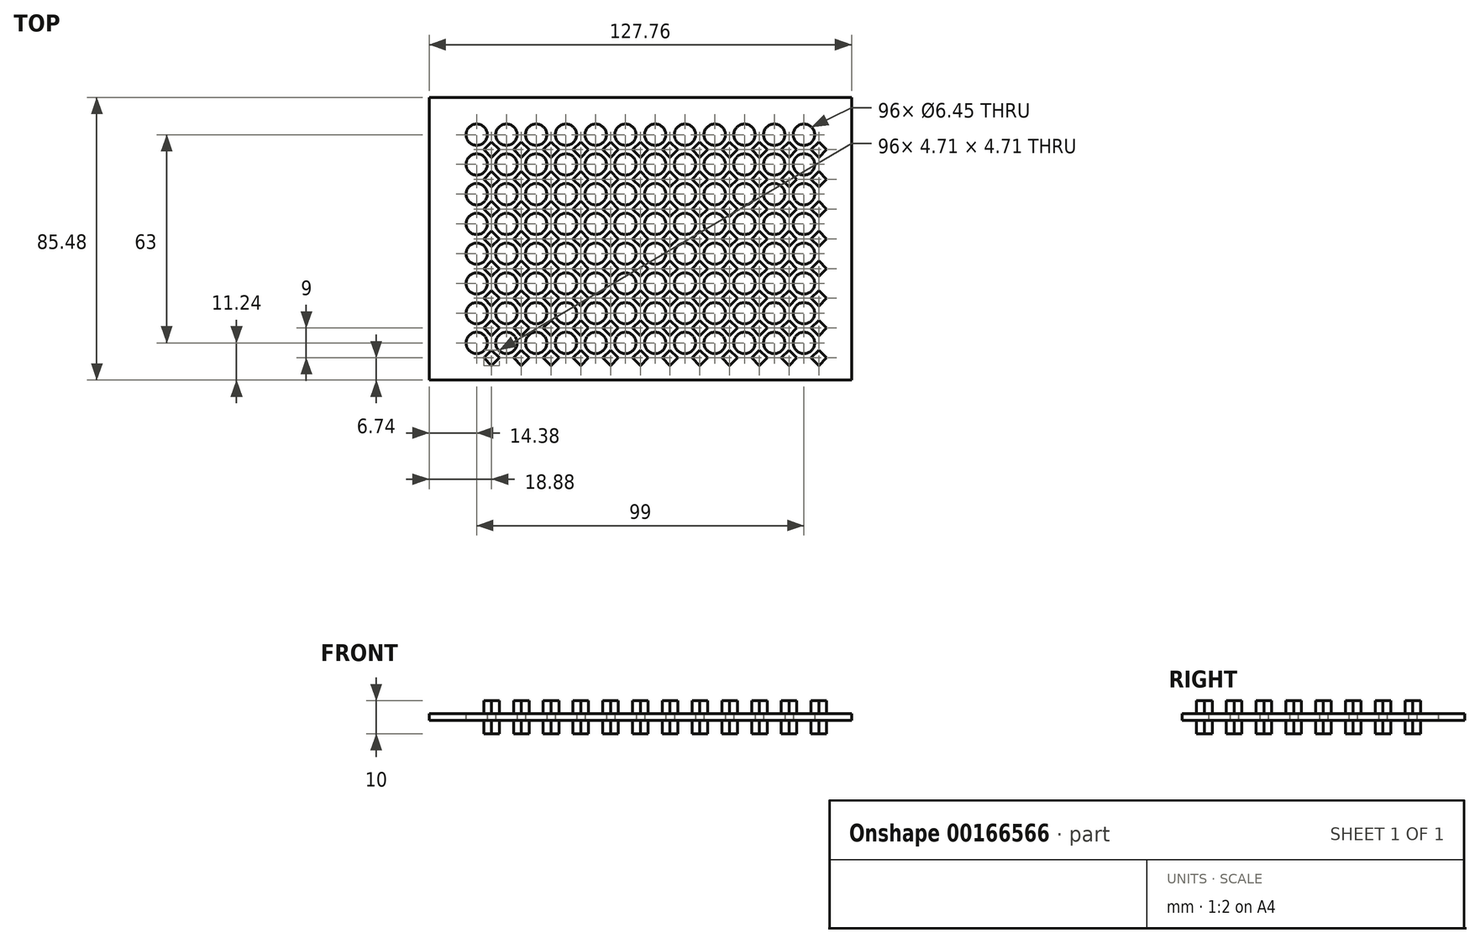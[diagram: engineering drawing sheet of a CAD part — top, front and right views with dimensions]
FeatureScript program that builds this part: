
annotation { "Feature Type Name" : "Feature", "Feature Type Description" : "" }
export const myFeature = defineFeature(function(context is Context, id is Id, definition is map)
    precondition{}
    {
        {
            var Q0;
            Q0=qCreatedBy(makeId("Top.planeOp"),FACE);
            var sketch = newSketch(context, id + "F0", { "sketchPlane" : qUnion([Q0])});
            skLineSegment(sketch, "E0.bottom", {"start": v(0, 0) * mm, "end": v(-127.76, 0) * mm});
            skLineSegment(sketch, "E0.top", {"start": v(0, 85.48) * mm, "end": v(-127.76, 85.48) * mm});
            skLineSegment(sketch, "E0.left", {"start": v(0, 0) * mm, "end": v(0, 85.48) * mm});
            skLineSegment(sketch, "E0.right", {"start": v(-127.76, 0) * mm, "end": v(-127.76, 85.48) * mm});
            skCircle(sketch, "E1", {"center": v(-113.38, 74.24) * mm, "radius": 3.23 * mm});
            skLineSegment(sketch, "E2.bottom", {"start": v(-119.17, 80.03) * mm, "end": v(-8.59, 80.03) * mm, "construction": true});
            skLineSegment(sketch, "E2.top", {"start": v(-119.17, 3.96) * mm, "end": v(-8.59, 3.96) * mm, "construction": true});
            skLineSegment(sketch, "E2.left", {"start": v(-119.17, 80.03) * mm, "end": v(-119.17, 3.96) * mm, "construction": true});
            skLineSegment(sketch, "E2.right", {"start": v(-8.59, 80.03) * mm, "end": v(-8.59, 3.96) * mm, "construction": true});
            skLineSegment(sketch, "E3", {"start": v(-113.38, 74.24) * mm, "end": v(-119.17, 74.24) * mm, "construction": true});
            skLineSegment(sketch, "E4", {"start": v(-119.17, 74.24) * mm, "end": v(-113.38, 74.24) * mm, "construction": true});
            skLineSegment(sketch, "E5", {"start": v(-113.38, 74.24) * mm, "end": v(-113.38, 80.03) * mm, "construction": true});
            skCircle(sketch, "E6.0.1.0", {"center": v(-113.38, 65.24) * mm, "radius": 3.23 * mm});
            skCircle(sketch, "E6.0.2.0", {"center": v(-113.38, 56.24) * mm, "radius": 3.23 * mm});
            skCircle(sketch, "E6.0.3.0", {"center": v(-113.38, 47.24) * mm, "radius": 3.23 * mm});
            skCircle(sketch, "E6.0.4.0", {"center": v(-113.38, 38.24) * mm, "radius": 3.23 * mm});
            skCircle(sketch, "E6.0.5.0", {"center": v(-113.38, 29.24) * mm, "radius": 3.23 * mm});
            skCircle(sketch, "E6.0.6.0", {"center": v(-113.38, 20.24) * mm, "radius": 3.23 * mm});
            skCircle(sketch, "E6.0.7.0", {"center": v(-113.38, 11.24) * mm, "radius": 3.23 * mm});
            skCircle(sketch, "E6.1.0.0", {"center": v(-104.38, 74.24) * mm, "radius": 3.23 * mm});
            skCircle(sketch, "E6.1.1.0", {"center": v(-104.38, 65.24) * mm, "radius": 3.23 * mm});
            skCircle(sketch, "E6.1.2.0", {"center": v(-104.38, 56.24) * mm, "radius": 3.23 * mm});
            skCircle(sketch, "E6.1.3.0", {"center": v(-104.38, 47.24) * mm, "radius": 3.23 * mm});
            skCircle(sketch, "E6.1.4.0", {"center": v(-104.38, 38.24) * mm, "radius": 3.23 * mm});
            skCircle(sketch, "E6.1.5.0", {"center": v(-104.38, 29.24) * mm, "radius": 3.23 * mm});
            skCircle(sketch, "E6.1.6.0", {"center": v(-104.38, 20.24) * mm, "radius": 3.23 * mm});
            skCircle(sketch, "E6.1.7.0", {"center": v(-104.38, 11.24) * mm, "radius": 3.23 * mm});
            skCircle(sketch, "E6.2.0.0", {"center": v(-95.38, 74.24) * mm, "radius": 3.23 * mm});
            skCircle(sketch, "E6.2.1.0", {"center": v(-95.38, 65.24) * mm, "radius": 3.23 * mm});
            skCircle(sketch, "E6.2.2.0", {"center": v(-95.38, 56.24) * mm, "radius": 3.23 * mm});
            skCircle(sketch, "E6.2.3.0", {"center": v(-95.38, 47.24) * mm, "radius": 3.23 * mm});
            skCircle(sketch, "E6.2.4.0", {"center": v(-95.38, 38.24) * mm, "radius": 3.23 * mm});
            skCircle(sketch, "E6.2.5.0", {"center": v(-95.38, 29.24) * mm, "radius": 3.23 * mm});
            skCircle(sketch, "E6.2.6.0", {"center": v(-95.38, 20.24) * mm, "radius": 3.23 * mm});
            skCircle(sketch, "E6.2.7.0", {"center": v(-95.38, 11.24) * mm, "radius": 3.23 * mm});
            skCircle(sketch, "E6.3.0.0", {"center": v(-86.38, 74.24) * mm, "radius": 3.23 * mm});
            skCircle(sketch, "E6.3.1.0", {"center": v(-86.38, 65.24) * mm, "radius": 3.23 * mm});
            skCircle(sketch, "E6.3.2.0", {"center": v(-86.38, 56.24) * mm, "radius": 3.23 * mm});
            skCircle(sketch, "E6.3.3.0", {"center": v(-86.38, 47.24) * mm, "radius": 3.23 * mm});
            skCircle(sketch, "E6.3.4.0", {"center": v(-86.38, 38.24) * mm, "radius": 3.23 * mm});
            skCircle(sketch, "E6.3.5.0", {"center": v(-86.38, 29.24) * mm, "radius": 3.23 * mm});
            skCircle(sketch, "E6.3.6.0", {"center": v(-86.38, 20.24) * mm, "radius": 3.23 * mm});
            skCircle(sketch, "E6.3.7.0", {"center": v(-86.38, 11.24) * mm, "radius": 3.23 * mm});
            skCircle(sketch, "E6.4.0.0", {"center": v(-77.38, 74.24) * mm, "radius": 3.23 * mm});
            skCircle(sketch, "E6.4.1.0", {"center": v(-77.38, 65.24) * mm, "radius": 3.23 * mm});
            skCircle(sketch, "E6.4.2.0", {"center": v(-77.38, 56.24) * mm, "radius": 3.23 * mm});
            skCircle(sketch, "E6.4.3.0", {"center": v(-77.38, 47.24) * mm, "radius": 3.23 * mm});
            skCircle(sketch, "E6.4.4.0", {"center": v(-77.38, 38.24) * mm, "radius": 3.23 * mm});
            skCircle(sketch, "E6.4.5.0", {"center": v(-77.38, 29.24) * mm, "radius": 3.23 * mm});
            skCircle(sketch, "E6.4.6.0", {"center": v(-77.38, 20.24) * mm, "radius": 3.23 * mm});
            skCircle(sketch, "E6.4.7.0", {"center": v(-77.38, 11.24) * mm, "radius": 3.23 * mm});
            skCircle(sketch, "E6.5.0.0", {"center": v(-68.38, 74.24) * mm, "radius": 3.23 * mm});
            skCircle(sketch, "E6.5.1.0", {"center": v(-68.38, 65.24) * mm, "radius": 3.23 * mm});
            skCircle(sketch, "E6.5.2.0", {"center": v(-68.38, 56.24) * mm, "radius": 3.23 * mm});
            skCircle(sketch, "E6.5.3.0", {"center": v(-68.38, 47.24) * mm, "radius": 3.23 * mm});
            skCircle(sketch, "E6.5.4.0", {"center": v(-68.38, 38.24) * mm, "radius": 3.23 * mm});
            skCircle(sketch, "E6.5.5.0", {"center": v(-68.38, 29.24) * mm, "radius": 3.23 * mm});
            skCircle(sketch, "E6.5.6.0", {"center": v(-68.38, 20.24) * mm, "radius": 3.23 * mm});
            skCircle(sketch, "E6.5.7.0", {"center": v(-68.38, 11.24) * mm, "radius": 3.23 * mm});
            skCircle(sketch, "E6.6.0.0", {"center": v(-59.38, 74.24) * mm, "radius": 3.23 * mm});
            skCircle(sketch, "E6.6.1.0", {"center": v(-59.38, 65.24) * mm, "radius": 3.23 * mm});
            skCircle(sketch, "E6.6.2.0", {"center": v(-59.38, 56.24) * mm, "radius": 3.23 * mm});
            skCircle(sketch, "E6.6.3.0", {"center": v(-59.38, 47.24) * mm, "radius": 3.23 * mm});
            skCircle(sketch, "E6.6.4.0", {"center": v(-59.38, 38.24) * mm, "radius": 3.23 * mm});
            skCircle(sketch, "E6.6.5.0", {"center": v(-59.38, 29.24) * mm, "radius": 3.23 * mm});
            skCircle(sketch, "E6.6.6.0", {"center": v(-59.38, 20.24) * mm, "radius": 3.23 * mm});
            skCircle(sketch, "E6.6.7.0", {"center": v(-59.38, 11.24) * mm, "radius": 3.23 * mm});
            skCircle(sketch, "E6.7.0.0", {"center": v(-50.38, 74.24) * mm, "radius": 3.23 * mm});
            skCircle(sketch, "E6.7.1.0", {"center": v(-50.38, 65.24) * mm, "radius": 3.23 * mm});
            skCircle(sketch, "E6.7.2.0", {"center": v(-50.38, 56.24) * mm, "radius": 3.23 * mm});
            skCircle(sketch, "E6.7.3.0", {"center": v(-50.38, 47.24) * mm, "radius": 3.23 * mm});
            skCircle(sketch, "E6.7.4.0", {"center": v(-50.38, 38.24) * mm, "radius": 3.23 * mm});
            skCircle(sketch, "E6.7.5.0", {"center": v(-50.38, 29.24) * mm, "radius": 3.23 * mm});
            skCircle(sketch, "E6.7.6.0", {"center": v(-50.38, 20.24) * mm, "radius": 3.23 * mm});
            skCircle(sketch, "E6.7.7.0", {"center": v(-50.38, 11.24) * mm, "radius": 3.23 * mm});
            skCircle(sketch, "E6.8.0.0", {"center": v(-41.38, 74.24) * mm, "radius": 3.23 * mm});
            skCircle(sketch, "E6.8.1.0", {"center": v(-41.38, 65.24) * mm, "radius": 3.23 * mm});
            skCircle(sketch, "E6.8.2.0", {"center": v(-41.38, 56.24) * mm, "radius": 3.23 * mm});
            skCircle(sketch, "E6.8.3.0", {"center": v(-41.38, 47.24) * mm, "radius": 3.23 * mm});
            skCircle(sketch, "E6.8.4.0", {"center": v(-41.38, 38.24) * mm, "radius": 3.23 * mm});
            skCircle(sketch, "E6.8.5.0", {"center": v(-41.38, 29.24) * mm, "radius": 3.23 * mm});
            skCircle(sketch, "E6.8.6.0", {"center": v(-41.38, 20.24) * mm, "radius": 3.23 * mm});
            skCircle(sketch, "E6.8.7.0", {"center": v(-41.38, 11.24) * mm, "radius": 3.23 * mm});
            skCircle(sketch, "E6.9.0.0", {"center": v(-32.38, 74.24) * mm, "radius": 3.23 * mm});
            skCircle(sketch, "E6.9.1.0", {"center": v(-32.38, 65.24) * mm, "radius": 3.23 * mm});
            skCircle(sketch, "E6.9.2.0", {"center": v(-32.38, 56.24) * mm, "radius": 3.23 * mm});
            skCircle(sketch, "E6.9.3.0", {"center": v(-32.38, 47.24) * mm, "radius": 3.23 * mm});
            skCircle(sketch, "E6.9.4.0", {"center": v(-32.38, 38.24) * mm, "radius": 3.23 * mm});
            skCircle(sketch, "E6.9.5.0", {"center": v(-32.38, 29.24) * mm, "radius": 3.23 * mm});
            skCircle(sketch, "E6.9.6.0", {"center": v(-32.38, 20.24) * mm, "radius": 3.23 * mm});
            skCircle(sketch, "E6.9.7.0", {"center": v(-32.38, 11.24) * mm, "radius": 3.23 * mm});
            skCircle(sketch, "E6.10.0.0", {"center": v(-23.38, 74.24) * mm, "radius": 3.23 * mm});
            skCircle(sketch, "E6.10.1.0", {"center": v(-23.38, 65.24) * mm, "radius": 3.23 * mm});
            skCircle(sketch, "E6.10.2.0", {"center": v(-23.38, 56.24) * mm, "radius": 3.23 * mm});
            skCircle(sketch, "E6.10.3.0", {"center": v(-23.38, 47.24) * mm, "radius": 3.23 * mm});
            skCircle(sketch, "E6.10.4.0", {"center": v(-23.38, 38.24) * mm, "radius": 3.23 * mm});
            skCircle(sketch, "E6.10.5.0", {"center": v(-23.38, 29.24) * mm, "radius": 3.23 * mm});
            skCircle(sketch, "E6.10.6.0", {"center": v(-23.38, 20.24) * mm, "radius": 3.23 * mm});
            skCircle(sketch, "E6.10.7.0", {"center": v(-23.38, 11.24) * mm, "radius": 3.23 * mm});
            skCircle(sketch, "E6.11.0.0", {"center": v(-14.38, 74.24) * mm, "radius": 3.23 * mm});
            skCircle(sketch, "E6.11.1.0", {"center": v(-14.38, 65.24) * mm, "radius": 3.23 * mm});
            skCircle(sketch, "E6.11.2.0", {"center": v(-14.38, 56.24) * mm, "radius": 3.23 * mm});
            skCircle(sketch, "E6.11.3.0", {"center": v(-14.38, 47.24) * mm, "radius": 3.23 * mm});
            skCircle(sketch, "E6.11.4.0", {"center": v(-14.38, 38.24) * mm, "radius": 3.23 * mm});
            skCircle(sketch, "E6.11.5.0", {"center": v(-14.38, 29.24) * mm, "radius": 3.23 * mm});
            skCircle(sketch, "E6.11.6.0", {"center": v(-14.38, 20.24) * mm, "radius": 3.23 * mm});
            skCircle(sketch, "E6.11.7.0", {"center": v(-14.38, 11.24) * mm, "radius": 3.23 * mm});
            skLineSegment(sketch, "E6.direction1", {"start": v(-113.38, 74.24) * mm, "end": v(-104.38, 74.24) * mm, "construction": true});
            skLineSegment(sketch, "E6.direction2", {"start": v(-113.38, 74.24) * mm, "end": v(-113.38, 65.24) * mm, "construction": true});
            skLineSegment(sketch, "E7", {"start": v(-119.17, 80.03) * mm, "end": v(-127.76, 80.03) * mm, "construction": true});
            skLineSegment(sketch, "E8", {"start": v(-8.59, 80.03) * mm, "end": v(0, 80.03) * mm, "construction": true});
            skLineSegment(sketch, "E9", {"start": v(-14.38, 74.24) * mm, "end": v(-14.38, 80.03) * mm, "construction": true});
            skLineSegment(sketch, "E10", {"start": v(-14.38, 74.24) * mm, "end": v(-8.59, 74.24) * mm, "construction": true});
            skSolve(sketch);
        }
        {
            var Q0;
            Q0 = qSketchRegion(id + "F0", true);
            extrude(context, id + "F1", {"entities" : qUnion([Q0]), "depth" : 1 * mm, "hasSecondDirection" : true, "secondDirectionOppositeDirection" : true, "secondDirectionDepth" : 1 * mm});
        }
        {
            var Q0;
            Q0=qCreatedBy(makeId("Top.planeOp"),FACE);
            var sketch = newSketch(context, id + "F2", { "sketchPlane" : qUnion([Q0])});
            skLineSegment(sketch, "E11", {"start": v(-108.88, 72.1) * mm, "end": v(-111.23, 69.74) * mm});
            skLineSegment(sketch, "E12", {"start": v(-111.23, 69.74) * mm, "end": v(-108.88, 67.39) * mm});
            skLineSegment(sketch, "E13", {"start": v(-108.88, 67.39) * mm, "end": v(-106.53, 69.74) * mm});
            skLineSegment(sketch, "E14", {"start": v(-106.53, 69.74) * mm, "end": v(-108.88, 72.1) * mm});
            skCircle(sketch, "E15", {"center": v(-113.38, 74.24) * mm, "radius": 3.23 * mm, "construction": true});
            skPoint(sketch, "E16", {"position": v(-113.38, 65.24) * mm});
            skPoint(sketch, "E17", {"position": v(-104.38, 74.24) * mm});
            skLineSegment(sketch, "E18", {"start": v(-113.38, 74.24) * mm, "end": v(-104.38, 74.24) * mm, "construction": true});
            skLineSegment(sketch, "E19", {"start": v(-113.38, 74.24) * mm, "end": v(-113.38, 65.24) * mm, "construction": true});
            skPoint(sketch, "E20", {"position": v(-113.38, 69.74) * mm});
            skPoint(sketch, "E21", {"position": v(-108.88, 74.24) * mm});
            skLineSegment(sketch, "E22", {"start": v(-110.06, 70.92) * mm, "end": v(-111.1, 71.96) * mm, "construction": true});
            skLineSegment(sketch, "E23.0.1.0", {"start": v(-111.23, 60.74) * mm, "end": v(-108.88, 58.39) * mm});
            skLineSegment(sketch, "E23.0.1.1", {"start": v(-108.88, 63.1) * mm, "end": v(-111.23, 60.74) * mm});
            skLineSegment(sketch, "E23.0.1.2", {"start": v(-106.53, 60.74) * mm, "end": v(-108.88, 63.1) * mm});
            skLineSegment(sketch, "E23.0.1.3", {"start": v(-108.88, 58.39) * mm, "end": v(-106.53, 60.74) * mm});
            skLineSegment(sketch, "E23.0.2.0", {"start": v(-111.23, 51.74) * mm, "end": v(-108.88, 49.39) * mm});
            skLineSegment(sketch, "E23.0.2.1", {"start": v(-108.88, 54.1) * mm, "end": v(-111.23, 51.74) * mm});
            skLineSegment(sketch, "E23.0.2.2", {"start": v(-106.53, 51.74) * mm, "end": v(-108.88, 54.1) * mm});
            skLineSegment(sketch, "E23.0.2.3", {"start": v(-108.88, 49.39) * mm, "end": v(-106.53, 51.74) * mm});
            skLineSegment(sketch, "E23.0.3.0", {"start": v(-111.23, 42.74) * mm, "end": v(-108.88, 40.39) * mm});
            skLineSegment(sketch, "E23.0.3.1", {"start": v(-108.88, 45.1) * mm, "end": v(-111.23, 42.74) * mm});
            skLineSegment(sketch, "E23.0.3.2", {"start": v(-106.53, 42.74) * mm, "end": v(-108.88, 45.1) * mm});
            skLineSegment(sketch, "E23.0.3.3", {"start": v(-108.88, 40.39) * mm, "end": v(-106.53, 42.74) * mm});
            skLineSegment(sketch, "E23.0.4.0", {"start": v(-111.23, 33.74) * mm, "end": v(-108.88, 31.39) * mm});
            skLineSegment(sketch, "E23.0.4.1", {"start": v(-108.88, 36.1) * mm, "end": v(-111.23, 33.74) * mm});
            skLineSegment(sketch, "E23.0.4.2", {"start": v(-106.53, 33.74) * mm, "end": v(-108.88, 36.1) * mm});
            skLineSegment(sketch, "E23.0.4.3", {"start": v(-108.88, 31.39) * mm, "end": v(-106.53, 33.74) * mm});
            skLineSegment(sketch, "E23.0.5.0", {"start": v(-111.23, 24.74) * mm, "end": v(-108.88, 22.39) * mm});
            skLineSegment(sketch, "E23.0.5.1", {"start": v(-108.88, 27.1) * mm, "end": v(-111.23, 24.74) * mm});
            skLineSegment(sketch, "E23.0.5.2", {"start": v(-106.53, 24.74) * mm, "end": v(-108.88, 27.1) * mm});
            skLineSegment(sketch, "E23.0.5.3", {"start": v(-108.88, 22.39) * mm, "end": v(-106.53, 24.74) * mm});
            skLineSegment(sketch, "E23.0.6.0", {"start": v(-111.23, 15.74) * mm, "end": v(-108.88, 13.39) * mm});
            skLineSegment(sketch, "E23.0.6.1", {"start": v(-108.88, 18.1) * mm, "end": v(-111.23, 15.74) * mm});
            skLineSegment(sketch, "E23.0.6.2", {"start": v(-106.53, 15.74) * mm, "end": v(-108.88, 18.1) * mm});
            skLineSegment(sketch, "E23.0.6.3", {"start": v(-108.88, 13.39) * mm, "end": v(-106.53, 15.74) * mm});
            skLineSegment(sketch, "E23.0.7.0", {"start": v(-111.23, 6.74) * mm, "end": v(-108.88, 4.39) * mm});
            skLineSegment(sketch, "E23.0.7.1", {"start": v(-108.88, 9.1) * mm, "end": v(-111.23, 6.74) * mm});
            skLineSegment(sketch, "E23.0.7.2", {"start": v(-106.53, 6.74) * mm, "end": v(-108.88, 9.1) * mm});
            skLineSegment(sketch, "E23.0.7.3", {"start": v(-108.88, 4.39) * mm, "end": v(-106.53, 6.74) * mm});
            skLineSegment(sketch, "E23.1.0.0", {"start": v(-102.23, 69.74) * mm, "end": v(-99.88, 67.39) * mm});
            skLineSegment(sketch, "E23.1.0.1", {"start": v(-99.88, 72.1) * mm, "end": v(-102.23, 69.74) * mm});
            skLineSegment(sketch, "E23.1.0.2", {"start": v(-97.53, 69.74) * mm, "end": v(-99.88, 72.1) * mm});
            skLineSegment(sketch, "E23.1.0.3", {"start": v(-99.88, 67.39) * mm, "end": v(-97.53, 69.74) * mm});
            skLineSegment(sketch, "E23.1.1.0", {"start": v(-102.23, 60.74) * mm, "end": v(-99.88, 58.39) * mm});
            skLineSegment(sketch, "E23.1.1.1", {"start": v(-99.88, 63.1) * mm, "end": v(-102.23, 60.74) * mm});
            skLineSegment(sketch, "E23.1.1.2", {"start": v(-97.53, 60.74) * mm, "end": v(-99.88, 63.1) * mm});
            skLineSegment(sketch, "E23.1.1.3", {"start": v(-99.88, 58.39) * mm, "end": v(-97.53, 60.74) * mm});
            skLineSegment(sketch, "E23.1.2.0", {"start": v(-102.23, 51.74) * mm, "end": v(-99.88, 49.39) * mm});
            skLineSegment(sketch, "E23.1.2.1", {"start": v(-99.88, 54.1) * mm, "end": v(-102.23, 51.74) * mm});
            skLineSegment(sketch, "E23.1.2.2", {"start": v(-97.53, 51.74) * mm, "end": v(-99.88, 54.1) * mm});
            skLineSegment(sketch, "E23.1.2.3", {"start": v(-99.88, 49.39) * mm, "end": v(-97.53, 51.74) * mm});
            skLineSegment(sketch, "E23.1.3.0", {"start": v(-102.23, 42.74) * mm, "end": v(-99.88, 40.39) * mm});
            skLineSegment(sketch, "E23.1.3.1", {"start": v(-99.88, 45.1) * mm, "end": v(-102.23, 42.74) * mm});
            skLineSegment(sketch, "E23.1.3.2", {"start": v(-97.53, 42.74) * mm, "end": v(-99.88, 45.1) * mm});
            skLineSegment(sketch, "E23.1.3.3", {"start": v(-99.88, 40.39) * mm, "end": v(-97.53, 42.74) * mm});
            skLineSegment(sketch, "E23.1.4.0", {"start": v(-102.23, 33.74) * mm, "end": v(-99.88, 31.39) * mm});
            skLineSegment(sketch, "E23.1.4.1", {"start": v(-99.88, 36.1) * mm, "end": v(-102.23, 33.74) * mm});
            skLineSegment(sketch, "E23.1.4.2", {"start": v(-97.53, 33.74) * mm, "end": v(-99.88, 36.1) * mm});
            skLineSegment(sketch, "E23.1.4.3", {"start": v(-99.88, 31.39) * mm, "end": v(-97.53, 33.74) * mm});
            skLineSegment(sketch, "E23.1.5.0", {"start": v(-102.23, 24.74) * mm, "end": v(-99.88, 22.39) * mm});
            skLineSegment(sketch, "E23.1.5.1", {"start": v(-99.88, 27.1) * mm, "end": v(-102.23, 24.74) * mm});
            skLineSegment(sketch, "E23.1.5.2", {"start": v(-97.53, 24.74) * mm, "end": v(-99.88, 27.1) * mm});
            skLineSegment(sketch, "E23.1.5.3", {"start": v(-99.88, 22.39) * mm, "end": v(-97.53, 24.74) * mm});
            skLineSegment(sketch, "E23.1.6.0", {"start": v(-102.23, 15.74) * mm, "end": v(-99.88, 13.39) * mm});
            skLineSegment(sketch, "E23.1.6.1", {"start": v(-99.88, 18.1) * mm, "end": v(-102.23, 15.74) * mm});
            skLineSegment(sketch, "E23.1.6.2", {"start": v(-97.53, 15.74) * mm, "end": v(-99.88, 18.1) * mm});
            skLineSegment(sketch, "E23.1.6.3", {"start": v(-99.88, 13.39) * mm, "end": v(-97.53, 15.74) * mm});
            skLineSegment(sketch, "E23.1.7.0", {"start": v(-102.23, 6.74) * mm, "end": v(-99.88, 4.39) * mm});
            skLineSegment(sketch, "E23.1.7.1", {"start": v(-99.88, 9.1) * mm, "end": v(-102.23, 6.74) * mm});
            skLineSegment(sketch, "E23.1.7.2", {"start": v(-97.53, 6.74) * mm, "end": v(-99.88, 9.1) * mm});
            skLineSegment(sketch, "E23.1.7.3", {"start": v(-99.88, 4.39) * mm, "end": v(-97.53, 6.74) * mm});
            skLineSegment(sketch, "E23.2.0.0", {"start": v(-93.23, 69.74) * mm, "end": v(-90.88, 67.39) * mm});
            skLineSegment(sketch, "E23.2.0.1", {"start": v(-90.88, 72.1) * mm, "end": v(-93.23, 69.74) * mm});
            skLineSegment(sketch, "E23.2.0.2", {"start": v(-88.53, 69.74) * mm, "end": v(-90.88, 72.1) * mm});
            skLineSegment(sketch, "E23.2.0.3", {"start": v(-90.88, 67.39) * mm, "end": v(-88.53, 69.74) * mm});
            skLineSegment(sketch, "E23.2.1.0", {"start": v(-93.23, 60.74) * mm, "end": v(-90.88, 58.39) * mm});
            skLineSegment(sketch, "E23.2.1.1", {"start": v(-90.88, 63.1) * mm, "end": v(-93.23, 60.74) * mm});
            skLineSegment(sketch, "E23.2.1.2", {"start": v(-88.53, 60.74) * mm, "end": v(-90.88, 63.1) * mm});
            skLineSegment(sketch, "E23.2.1.3", {"start": v(-90.88, 58.39) * mm, "end": v(-88.53, 60.74) * mm});
            skLineSegment(sketch, "E23.2.2.0", {"start": v(-93.23, 51.74) * mm, "end": v(-90.88, 49.39) * mm});
            skLineSegment(sketch, "E23.2.2.1", {"start": v(-90.88, 54.1) * mm, "end": v(-93.23, 51.74) * mm});
            skLineSegment(sketch, "E23.2.2.2", {"start": v(-88.53, 51.74) * mm, "end": v(-90.88, 54.1) * mm});
            skLineSegment(sketch, "E23.2.2.3", {"start": v(-90.88, 49.39) * mm, "end": v(-88.53, 51.74) * mm});
            skLineSegment(sketch, "E23.2.3.0", {"start": v(-93.23, 42.74) * mm, "end": v(-90.88, 40.39) * mm});
            skLineSegment(sketch, "E23.2.3.1", {"start": v(-90.88, 45.1) * mm, "end": v(-93.23, 42.74) * mm});
            skLineSegment(sketch, "E23.2.3.2", {"start": v(-88.53, 42.74) * mm, "end": v(-90.88, 45.1) * mm});
            skLineSegment(sketch, "E23.2.3.3", {"start": v(-90.88, 40.39) * mm, "end": v(-88.53, 42.74) * mm});
            skLineSegment(sketch, "E23.2.4.0", {"start": v(-93.23, 33.74) * mm, "end": v(-90.88, 31.39) * mm});
            skLineSegment(sketch, "E23.2.4.1", {"start": v(-90.88, 36.1) * mm, "end": v(-93.23, 33.74) * mm});
            skLineSegment(sketch, "E23.2.4.2", {"start": v(-88.53, 33.74) * mm, "end": v(-90.88, 36.1) * mm});
            skLineSegment(sketch, "E23.2.4.3", {"start": v(-90.88, 31.39) * mm, "end": v(-88.53, 33.74) * mm});
            skLineSegment(sketch, "E23.2.5.0", {"start": v(-93.23, 24.74) * mm, "end": v(-90.88, 22.39) * mm});
            skLineSegment(sketch, "E23.2.5.1", {"start": v(-90.88, 27.1) * mm, "end": v(-93.23, 24.74) * mm});
            skLineSegment(sketch, "E23.2.5.2", {"start": v(-88.53, 24.74) * mm, "end": v(-90.88, 27.1) * mm});
            skLineSegment(sketch, "E23.2.5.3", {"start": v(-90.88, 22.39) * mm, "end": v(-88.53, 24.74) * mm});
            skLineSegment(sketch, "E23.2.6.0", {"start": v(-93.23, 15.74) * mm, "end": v(-90.88, 13.39) * mm});
            skLineSegment(sketch, "E23.2.6.1", {"start": v(-90.88, 18.1) * mm, "end": v(-93.23, 15.74) * mm});
            skLineSegment(sketch, "E23.2.6.2", {"start": v(-88.53, 15.74) * mm, "end": v(-90.88, 18.1) * mm});
            skLineSegment(sketch, "E23.2.6.3", {"start": v(-90.88, 13.39) * mm, "end": v(-88.53, 15.74) * mm});
            skLineSegment(sketch, "E23.2.7.0", {"start": v(-93.23, 6.74) * mm, "end": v(-90.88, 4.39) * mm});
            skLineSegment(sketch, "E23.2.7.1", {"start": v(-90.88, 9.1) * mm, "end": v(-93.23, 6.74) * mm});
            skLineSegment(sketch, "E23.2.7.2", {"start": v(-88.53, 6.74) * mm, "end": v(-90.88, 9.1) * mm});
            skLineSegment(sketch, "E23.2.7.3", {"start": v(-90.88, 4.39) * mm, "end": v(-88.53, 6.74) * mm});
            skLineSegment(sketch, "E23.3.0.0", {"start": v(-84.23, 69.74) * mm, "end": v(-81.88, 67.39) * mm});
            skLineSegment(sketch, "E23.3.0.1", {"start": v(-81.88, 72.1) * mm, "end": v(-84.23, 69.74) * mm});
            skLineSegment(sketch, "E23.3.0.2", {"start": v(-79.53, 69.74) * mm, "end": v(-81.88, 72.1) * mm});
            skLineSegment(sketch, "E23.3.0.3", {"start": v(-81.88, 67.39) * mm, "end": v(-79.53, 69.74) * mm});
            skLineSegment(sketch, "E23.3.1.0", {"start": v(-84.23, 60.74) * mm, "end": v(-81.88, 58.39) * mm});
            skLineSegment(sketch, "E23.3.1.1", {"start": v(-81.88, 63.1) * mm, "end": v(-84.23, 60.74) * mm});
            skLineSegment(sketch, "E23.3.1.2", {"start": v(-79.53, 60.74) * mm, "end": v(-81.88, 63.1) * mm});
            skLineSegment(sketch, "E23.3.1.3", {"start": v(-81.88, 58.39) * mm, "end": v(-79.53, 60.74) * mm});
            skLineSegment(sketch, "E23.3.2.0", {"start": v(-84.23, 51.74) * mm, "end": v(-81.88, 49.39) * mm});
            skLineSegment(sketch, "E23.3.2.1", {"start": v(-81.88, 54.1) * mm, "end": v(-84.23, 51.74) * mm});
            skLineSegment(sketch, "E23.3.2.2", {"start": v(-79.53, 51.74) * mm, "end": v(-81.88, 54.1) * mm});
            skLineSegment(sketch, "E23.3.2.3", {"start": v(-81.88, 49.39) * mm, "end": v(-79.53, 51.74) * mm});
            skLineSegment(sketch, "E23.3.3.0", {"start": v(-84.23, 42.74) * mm, "end": v(-81.88, 40.39) * mm});
            skLineSegment(sketch, "E23.3.3.1", {"start": v(-81.88, 45.1) * mm, "end": v(-84.23, 42.74) * mm});
            skLineSegment(sketch, "E23.3.3.2", {"start": v(-79.53, 42.74) * mm, "end": v(-81.88, 45.1) * mm});
            skLineSegment(sketch, "E23.3.3.3", {"start": v(-81.88, 40.39) * mm, "end": v(-79.53, 42.74) * mm});
            skLineSegment(sketch, "E23.3.4.0", {"start": v(-84.23, 33.74) * mm, "end": v(-81.88, 31.39) * mm});
            skLineSegment(sketch, "E23.3.4.1", {"start": v(-81.88, 36.1) * mm, "end": v(-84.23, 33.74) * mm});
            skLineSegment(sketch, "E23.3.4.2", {"start": v(-79.53, 33.74) * mm, "end": v(-81.88, 36.1) * mm});
            skLineSegment(sketch, "E23.3.4.3", {"start": v(-81.88, 31.39) * mm, "end": v(-79.53, 33.74) * mm});
            skLineSegment(sketch, "E23.3.5.0", {"start": v(-84.23, 24.74) * mm, "end": v(-81.88, 22.39) * mm});
            skLineSegment(sketch, "E23.3.5.1", {"start": v(-81.88, 27.1) * mm, "end": v(-84.23, 24.74) * mm});
            skLineSegment(sketch, "E23.3.5.2", {"start": v(-79.53, 24.74) * mm, "end": v(-81.88, 27.1) * mm});
            skLineSegment(sketch, "E23.3.5.3", {"start": v(-81.88, 22.39) * mm, "end": v(-79.53, 24.74) * mm});
            skLineSegment(sketch, "E23.3.6.0", {"start": v(-84.23, 15.74) * mm, "end": v(-81.88, 13.39) * mm});
            skLineSegment(sketch, "E23.3.6.1", {"start": v(-81.88, 18.1) * mm, "end": v(-84.23, 15.74) * mm});
            skLineSegment(sketch, "E23.3.6.2", {"start": v(-79.53, 15.74) * mm, "end": v(-81.88, 18.1) * mm});
            skLineSegment(sketch, "E23.3.6.3", {"start": v(-81.88, 13.39) * mm, "end": v(-79.53, 15.74) * mm});
            skLineSegment(sketch, "E23.3.7.0", {"start": v(-84.23, 6.74) * mm, "end": v(-81.88, 4.39) * mm});
            skLineSegment(sketch, "E23.3.7.1", {"start": v(-81.88, 9.1) * mm, "end": v(-84.23, 6.74) * mm});
            skLineSegment(sketch, "E23.3.7.2", {"start": v(-79.53, 6.74) * mm, "end": v(-81.88, 9.1) * mm});
            skLineSegment(sketch, "E23.3.7.3", {"start": v(-81.88, 4.39) * mm, "end": v(-79.53, 6.74) * mm});
            skLineSegment(sketch, "E23.4.0.0", {"start": v(-75.23, 69.74) * mm, "end": v(-72.88, 67.39) * mm});
            skLineSegment(sketch, "E23.4.0.1", {"start": v(-72.88, 72.1) * mm, "end": v(-75.23, 69.74) * mm});
            skLineSegment(sketch, "E23.4.0.2", {"start": v(-70.53, 69.74) * mm, "end": v(-72.88, 72.1) * mm});
            skLineSegment(sketch, "E23.4.0.3", {"start": v(-72.88, 67.39) * mm, "end": v(-70.53, 69.74) * mm});
            skLineSegment(sketch, "E23.4.1.0", {"start": v(-75.23, 60.74) * mm, "end": v(-72.88, 58.39) * mm});
            skLineSegment(sketch, "E23.4.1.1", {"start": v(-72.88, 63.1) * mm, "end": v(-75.23, 60.74) * mm});
            skLineSegment(sketch, "E23.4.1.2", {"start": v(-70.53, 60.74) * mm, "end": v(-72.88, 63.1) * mm});
            skLineSegment(sketch, "E23.4.1.3", {"start": v(-72.88, 58.39) * mm, "end": v(-70.53, 60.74) * mm});
            skLineSegment(sketch, "E23.4.2.0", {"start": v(-75.23, 51.74) * mm, "end": v(-72.88, 49.39) * mm});
            skLineSegment(sketch, "E23.4.2.1", {"start": v(-72.88, 54.1) * mm, "end": v(-75.23, 51.74) * mm});
            skLineSegment(sketch, "E23.4.2.2", {"start": v(-70.53, 51.74) * mm, "end": v(-72.88, 54.1) * mm});
            skLineSegment(sketch, "E23.4.2.3", {"start": v(-72.88, 49.39) * mm, "end": v(-70.53, 51.74) * mm});
            skLineSegment(sketch, "E23.4.3.0", {"start": v(-75.23, 42.74) * mm, "end": v(-72.88, 40.39) * mm});
            skLineSegment(sketch, "E23.4.3.1", {"start": v(-72.88, 45.1) * mm, "end": v(-75.23, 42.74) * mm});
            skLineSegment(sketch, "E23.4.3.2", {"start": v(-70.53, 42.74) * mm, "end": v(-72.88, 45.1) * mm});
            skLineSegment(sketch, "E23.4.3.3", {"start": v(-72.88, 40.39) * mm, "end": v(-70.53, 42.74) * mm});
            skLineSegment(sketch, "E23.4.4.0", {"start": v(-75.23, 33.74) * mm, "end": v(-72.88, 31.39) * mm});
            skLineSegment(sketch, "E23.4.4.1", {"start": v(-72.88, 36.1) * mm, "end": v(-75.23, 33.74) * mm});
            skLineSegment(sketch, "E23.4.4.2", {"start": v(-70.53, 33.74) * mm, "end": v(-72.88, 36.1) * mm});
            skLineSegment(sketch, "E23.4.4.3", {"start": v(-72.88, 31.39) * mm, "end": v(-70.53, 33.74) * mm});
            skLineSegment(sketch, "E23.4.5.0", {"start": v(-75.23, 24.74) * mm, "end": v(-72.88, 22.39) * mm});
            skLineSegment(sketch, "E23.4.5.1", {"start": v(-72.88, 27.1) * mm, "end": v(-75.23, 24.74) * mm});
            skLineSegment(sketch, "E23.4.5.2", {"start": v(-70.53, 24.74) * mm, "end": v(-72.88, 27.1) * mm});
            skLineSegment(sketch, "E23.4.5.3", {"start": v(-72.88, 22.39) * mm, "end": v(-70.53, 24.74) * mm});
            skLineSegment(sketch, "E23.4.6.0", {"start": v(-75.23, 15.74) * mm, "end": v(-72.88, 13.39) * mm});
            skLineSegment(sketch, "E23.4.6.1", {"start": v(-72.88, 18.1) * mm, "end": v(-75.23, 15.74) * mm});
            skLineSegment(sketch, "E23.4.6.2", {"start": v(-70.53, 15.74) * mm, "end": v(-72.88, 18.1) * mm});
            skLineSegment(sketch, "E23.4.6.3", {"start": v(-72.88, 13.39) * mm, "end": v(-70.53, 15.74) * mm});
            skLineSegment(sketch, "E23.4.7.0", {"start": v(-75.23, 6.74) * mm, "end": v(-72.88, 4.39) * mm});
            skLineSegment(sketch, "E23.4.7.1", {"start": v(-72.88, 9.1) * mm, "end": v(-75.23, 6.74) * mm});
            skLineSegment(sketch, "E23.4.7.2", {"start": v(-70.53, 6.74) * mm, "end": v(-72.88, 9.1) * mm});
            skLineSegment(sketch, "E23.4.7.3", {"start": v(-72.88, 4.39) * mm, "end": v(-70.53, 6.74) * mm});
            skLineSegment(sketch, "E23.5.0.0", {"start": v(-66.23, 69.74) * mm, "end": v(-63.88, 67.39) * mm});
            skLineSegment(sketch, "E23.5.0.1", {"start": v(-63.88, 72.1) * mm, "end": v(-66.23, 69.74) * mm});
            skLineSegment(sketch, "E23.5.0.2", {"start": v(-61.53, 69.74) * mm, "end": v(-63.88, 72.1) * mm});
            skLineSegment(sketch, "E23.5.0.3", {"start": v(-63.88, 67.39) * mm, "end": v(-61.53, 69.74) * mm});
            skLineSegment(sketch, "E23.5.1.0", {"start": v(-66.23, 60.74) * mm, "end": v(-63.88, 58.39) * mm});
            skLineSegment(sketch, "E23.5.1.1", {"start": v(-63.88, 63.1) * mm, "end": v(-66.23, 60.74) * mm});
            skLineSegment(sketch, "E23.5.1.2", {"start": v(-61.53, 60.74) * mm, "end": v(-63.88, 63.1) * mm});
            skLineSegment(sketch, "E23.5.1.3", {"start": v(-63.88, 58.39) * mm, "end": v(-61.53, 60.74) * mm});
            skLineSegment(sketch, "E23.5.2.0", {"start": v(-66.23, 51.74) * mm, "end": v(-63.88, 49.39) * mm});
            skLineSegment(sketch, "E23.5.2.1", {"start": v(-63.88, 54.1) * mm, "end": v(-66.23, 51.74) * mm});
            skLineSegment(sketch, "E23.5.2.2", {"start": v(-61.53, 51.74) * mm, "end": v(-63.88, 54.1) * mm});
            skLineSegment(sketch, "E23.5.2.3", {"start": v(-63.88, 49.39) * mm, "end": v(-61.53, 51.74) * mm});
            skLineSegment(sketch, "E23.5.3.0", {"start": v(-66.23, 42.74) * mm, "end": v(-63.88, 40.39) * mm});
            skLineSegment(sketch, "E23.5.3.1", {"start": v(-63.88, 45.1) * mm, "end": v(-66.23, 42.74) * mm});
            skLineSegment(sketch, "E23.5.3.2", {"start": v(-61.53, 42.74) * mm, "end": v(-63.88, 45.1) * mm});
            skLineSegment(sketch, "E23.5.3.3", {"start": v(-63.88, 40.39) * mm, "end": v(-61.53, 42.74) * mm});
            skLineSegment(sketch, "E23.5.4.0", {"start": v(-66.23, 33.74) * mm, "end": v(-63.88, 31.39) * mm});
            skLineSegment(sketch, "E23.5.4.1", {"start": v(-63.88, 36.1) * mm, "end": v(-66.23, 33.74) * mm});
            skLineSegment(sketch, "E23.5.4.2", {"start": v(-61.53, 33.74) * mm, "end": v(-63.88, 36.1) * mm});
            skLineSegment(sketch, "E23.5.4.3", {"start": v(-63.88, 31.39) * mm, "end": v(-61.53, 33.74) * mm});
            skLineSegment(sketch, "E23.5.5.0", {"start": v(-66.23, 24.74) * mm, "end": v(-63.88, 22.39) * mm});
            skLineSegment(sketch, "E23.5.5.1", {"start": v(-63.88, 27.1) * mm, "end": v(-66.23, 24.74) * mm});
            skLineSegment(sketch, "E23.5.5.2", {"start": v(-61.53, 24.74) * mm, "end": v(-63.88, 27.1) * mm});
            skLineSegment(sketch, "E23.5.5.3", {"start": v(-63.88, 22.39) * mm, "end": v(-61.53, 24.74) * mm});
            skLineSegment(sketch, "E23.5.6.0", {"start": v(-66.23, 15.74) * mm, "end": v(-63.88, 13.39) * mm});
            skLineSegment(sketch, "E23.5.6.1", {"start": v(-63.88, 18.1) * mm, "end": v(-66.23, 15.74) * mm});
            skLineSegment(sketch, "E23.5.6.2", {"start": v(-61.53, 15.74) * mm, "end": v(-63.88, 18.1) * mm});
            skLineSegment(sketch, "E23.5.6.3", {"start": v(-63.88, 13.39) * mm, "end": v(-61.53, 15.74) * mm});
            skLineSegment(sketch, "E23.5.7.0", {"start": v(-66.23, 6.74) * mm, "end": v(-63.88, 4.39) * mm});
            skLineSegment(sketch, "E23.5.7.1", {"start": v(-63.88, 9.1) * mm, "end": v(-66.23, 6.74) * mm});
            skLineSegment(sketch, "E23.5.7.2", {"start": v(-61.53, 6.74) * mm, "end": v(-63.88, 9.1) * mm});
            skLineSegment(sketch, "E23.5.7.3", {"start": v(-63.88, 4.39) * mm, "end": v(-61.53, 6.74) * mm});
            skLineSegment(sketch, "E23.6.0.0", {"start": v(-57.23, 69.74) * mm, "end": v(-54.88, 67.39) * mm});
            skLineSegment(sketch, "E23.6.0.1", {"start": v(-54.88, 72.1) * mm, "end": v(-57.23, 69.74) * mm});
            skLineSegment(sketch, "E23.6.0.2", {"start": v(-52.53, 69.74) * mm, "end": v(-54.88, 72.1) * mm});
            skLineSegment(sketch, "E23.6.0.3", {"start": v(-54.88, 67.39) * mm, "end": v(-52.53, 69.74) * mm});
            skLineSegment(sketch, "E23.6.1.0", {"start": v(-57.23, 60.74) * mm, "end": v(-54.88, 58.39) * mm});
            skLineSegment(sketch, "E23.6.1.1", {"start": v(-54.88, 63.1) * mm, "end": v(-57.23, 60.74) * mm});
            skLineSegment(sketch, "E23.6.1.2", {"start": v(-52.53, 60.74) * mm, "end": v(-54.88, 63.1) * mm});
            skLineSegment(sketch, "E23.6.1.3", {"start": v(-54.88, 58.39) * mm, "end": v(-52.53, 60.74) * mm});
            skLineSegment(sketch, "E23.6.2.0", {"start": v(-57.23, 51.74) * mm, "end": v(-54.88, 49.39) * mm});
            skLineSegment(sketch, "E23.6.2.1", {"start": v(-54.88, 54.1) * mm, "end": v(-57.23, 51.74) * mm});
            skLineSegment(sketch, "E23.6.2.2", {"start": v(-52.53, 51.74) * mm, "end": v(-54.88, 54.1) * mm});
            skLineSegment(sketch, "E23.6.2.3", {"start": v(-54.88, 49.39) * mm, "end": v(-52.53, 51.74) * mm});
            skLineSegment(sketch, "E23.6.3.0", {"start": v(-57.23, 42.74) * mm, "end": v(-54.88, 40.39) * mm});
            skLineSegment(sketch, "E23.6.3.1", {"start": v(-54.88, 45.1) * mm, "end": v(-57.23, 42.74) * mm});
            skLineSegment(sketch, "E23.6.3.2", {"start": v(-52.53, 42.74) * mm, "end": v(-54.88, 45.1) * mm});
            skLineSegment(sketch, "E23.6.3.3", {"start": v(-54.88, 40.39) * mm, "end": v(-52.53, 42.74) * mm});
            skLineSegment(sketch, "E23.6.4.0", {"start": v(-57.23, 33.74) * mm, "end": v(-54.88, 31.39) * mm});
            skLineSegment(sketch, "E23.6.4.1", {"start": v(-54.88, 36.1) * mm, "end": v(-57.23, 33.74) * mm});
            skLineSegment(sketch, "E23.6.4.2", {"start": v(-52.53, 33.74) * mm, "end": v(-54.88, 36.1) * mm});
            skLineSegment(sketch, "E23.6.4.3", {"start": v(-54.88, 31.39) * mm, "end": v(-52.53, 33.74) * mm});
            skLineSegment(sketch, "E23.6.5.0", {"start": v(-57.23, 24.74) * mm, "end": v(-54.88, 22.39) * mm});
            skLineSegment(sketch, "E23.6.5.1", {"start": v(-54.88, 27.1) * mm, "end": v(-57.23, 24.74) * mm});
            skLineSegment(sketch, "E23.6.5.2", {"start": v(-52.53, 24.74) * mm, "end": v(-54.88, 27.1) * mm});
            skLineSegment(sketch, "E23.6.5.3", {"start": v(-54.88, 22.39) * mm, "end": v(-52.53, 24.74) * mm});
            skLineSegment(sketch, "E23.6.6.0", {"start": v(-57.23, 15.74) * mm, "end": v(-54.88, 13.39) * mm});
            skLineSegment(sketch, "E23.6.6.1", {"start": v(-54.88, 18.1) * mm, "end": v(-57.23, 15.74) * mm});
            skLineSegment(sketch, "E23.6.6.2", {"start": v(-52.53, 15.74) * mm, "end": v(-54.88, 18.1) * mm});
            skLineSegment(sketch, "E23.6.6.3", {"start": v(-54.88, 13.39) * mm, "end": v(-52.53, 15.74) * mm});
            skLineSegment(sketch, "E23.6.7.0", {"start": v(-57.23, 6.74) * mm, "end": v(-54.88, 4.39) * mm});
            skLineSegment(sketch, "E23.6.7.1", {"start": v(-54.88, 9.1) * mm, "end": v(-57.23, 6.74) * mm});
            skLineSegment(sketch, "E23.6.7.2", {"start": v(-52.53, 6.74) * mm, "end": v(-54.88, 9.1) * mm});
            skLineSegment(sketch, "E23.6.7.3", {"start": v(-54.88, 4.39) * mm, "end": v(-52.53, 6.74) * mm});
            skLineSegment(sketch, "E23.7.0.0", {"start": v(-48.23, 69.74) * mm, "end": v(-45.88, 67.39) * mm});
            skLineSegment(sketch, "E23.7.0.1", {"start": v(-45.88, 72.1) * mm, "end": v(-48.23, 69.74) * mm});
            skLineSegment(sketch, "E23.7.0.2", {"start": v(-43.53, 69.74) * mm, "end": v(-45.88, 72.1) * mm});
            skLineSegment(sketch, "E23.7.0.3", {"start": v(-45.88, 67.39) * mm, "end": v(-43.53, 69.74) * mm});
            skLineSegment(sketch, "E23.7.1.0", {"start": v(-48.23, 60.74) * mm, "end": v(-45.88, 58.39) * mm});
            skLineSegment(sketch, "E23.7.1.1", {"start": v(-45.88, 63.1) * mm, "end": v(-48.23, 60.74) * mm});
            skLineSegment(sketch, "E23.7.1.2", {"start": v(-43.53, 60.74) * mm, "end": v(-45.88, 63.1) * mm});
            skLineSegment(sketch, "E23.7.1.3", {"start": v(-45.88, 58.39) * mm, "end": v(-43.53, 60.74) * mm});
            skLineSegment(sketch, "E23.7.2.0", {"start": v(-48.23, 51.74) * mm, "end": v(-45.88, 49.39) * mm});
            skLineSegment(sketch, "E23.7.2.1", {"start": v(-45.88, 54.1) * mm, "end": v(-48.23, 51.74) * mm});
            skLineSegment(sketch, "E23.7.2.2", {"start": v(-43.53, 51.74) * mm, "end": v(-45.88, 54.1) * mm});
            skLineSegment(sketch, "E23.7.2.3", {"start": v(-45.88, 49.39) * mm, "end": v(-43.53, 51.74) * mm});
            skLineSegment(sketch, "E23.7.3.0", {"start": v(-48.23, 42.74) * mm, "end": v(-45.88, 40.39) * mm});
            skLineSegment(sketch, "E23.7.3.1", {"start": v(-45.88, 45.1) * mm, "end": v(-48.23, 42.74) * mm});
            skLineSegment(sketch, "E23.7.3.2", {"start": v(-43.53, 42.74) * mm, "end": v(-45.88, 45.1) * mm});
            skLineSegment(sketch, "E23.7.3.3", {"start": v(-45.88, 40.39) * mm, "end": v(-43.53, 42.74) * mm});
            skLineSegment(sketch, "E23.7.4.0", {"start": v(-48.23, 33.74) * mm, "end": v(-45.88, 31.39) * mm});
            skLineSegment(sketch, "E23.7.4.1", {"start": v(-45.88, 36.1) * mm, "end": v(-48.23, 33.74) * mm});
            skLineSegment(sketch, "E23.7.4.2", {"start": v(-43.53, 33.74) * mm, "end": v(-45.88, 36.1) * mm});
            skLineSegment(sketch, "E23.7.4.3", {"start": v(-45.88, 31.39) * mm, "end": v(-43.53, 33.74) * mm});
            skLineSegment(sketch, "E23.7.5.0", {"start": v(-48.23, 24.74) * mm, "end": v(-45.88, 22.39) * mm});
            skLineSegment(sketch, "E23.7.5.1", {"start": v(-45.88, 27.1) * mm, "end": v(-48.23, 24.74) * mm});
            skLineSegment(sketch, "E23.7.5.2", {"start": v(-43.53, 24.74) * mm, "end": v(-45.88, 27.1) * mm});
            skLineSegment(sketch, "E23.7.5.3", {"start": v(-45.88, 22.39) * mm, "end": v(-43.53, 24.74) * mm});
            skLineSegment(sketch, "E23.7.6.0", {"start": v(-48.23, 15.74) * mm, "end": v(-45.88, 13.39) * mm});
            skLineSegment(sketch, "E23.7.6.1", {"start": v(-45.88, 18.1) * mm, "end": v(-48.23, 15.74) * mm});
            skLineSegment(sketch, "E23.7.6.2", {"start": v(-43.53, 15.74) * mm, "end": v(-45.88, 18.1) * mm});
            skLineSegment(sketch, "E23.7.6.3", {"start": v(-45.88, 13.39) * mm, "end": v(-43.53, 15.74) * mm});
            skLineSegment(sketch, "E23.7.7.0", {"start": v(-48.23, 6.74) * mm, "end": v(-45.88, 4.39) * mm});
            skLineSegment(sketch, "E23.7.7.1", {"start": v(-45.88, 9.1) * mm, "end": v(-48.23, 6.74) * mm});
            skLineSegment(sketch, "E23.7.7.2", {"start": v(-43.53, 6.74) * mm, "end": v(-45.88, 9.1) * mm});
            skLineSegment(sketch, "E23.7.7.3", {"start": v(-45.88, 4.39) * mm, "end": v(-43.53, 6.74) * mm});
            skLineSegment(sketch, "E23.8.0.0", {"start": v(-39.23, 69.74) * mm, "end": v(-36.88, 67.39) * mm});
            skLineSegment(sketch, "E23.8.0.1", {"start": v(-36.88, 72.1) * mm, "end": v(-39.23, 69.74) * mm});
            skLineSegment(sketch, "E23.8.0.2", {"start": v(-34.53, 69.74) * mm, "end": v(-36.88, 72.1) * mm});
            skLineSegment(sketch, "E23.8.0.3", {"start": v(-36.88, 67.39) * mm, "end": v(-34.53, 69.74) * mm});
            skLineSegment(sketch, "E23.8.1.0", {"start": v(-39.23, 60.74) * mm, "end": v(-36.88, 58.39) * mm});
            skLineSegment(sketch, "E23.8.1.1", {"start": v(-36.88, 63.1) * mm, "end": v(-39.23, 60.74) * mm});
            skLineSegment(sketch, "E23.8.1.2", {"start": v(-34.53, 60.74) * mm, "end": v(-36.88, 63.1) * mm});
            skLineSegment(sketch, "E23.8.1.3", {"start": v(-36.88, 58.39) * mm, "end": v(-34.53, 60.74) * mm});
            skLineSegment(sketch, "E23.8.2.0", {"start": v(-39.23, 51.74) * mm, "end": v(-36.88, 49.39) * mm});
            skLineSegment(sketch, "E23.8.2.1", {"start": v(-36.88, 54.1) * mm, "end": v(-39.23, 51.74) * mm});
            skLineSegment(sketch, "E23.8.2.2", {"start": v(-34.53, 51.74) * mm, "end": v(-36.88, 54.1) * mm});
            skLineSegment(sketch, "E23.8.2.3", {"start": v(-36.88, 49.39) * mm, "end": v(-34.53, 51.74) * mm});
            skLineSegment(sketch, "E23.8.3.0", {"start": v(-39.23, 42.74) * mm, "end": v(-36.88, 40.39) * mm});
            skLineSegment(sketch, "E23.8.3.1", {"start": v(-36.88, 45.1) * mm, "end": v(-39.23, 42.74) * mm});
            skLineSegment(sketch, "E23.8.3.2", {"start": v(-34.53, 42.74) * mm, "end": v(-36.88, 45.1) * mm});
            skLineSegment(sketch, "E23.8.3.3", {"start": v(-36.88, 40.39) * mm, "end": v(-34.53, 42.74) * mm});
            skLineSegment(sketch, "E23.8.4.0", {"start": v(-39.23, 33.74) * mm, "end": v(-36.88, 31.39) * mm});
            skLineSegment(sketch, "E23.8.4.1", {"start": v(-36.88, 36.1) * mm, "end": v(-39.23, 33.74) * mm});
            skLineSegment(sketch, "E23.8.4.2", {"start": v(-34.53, 33.74) * mm, "end": v(-36.88, 36.1) * mm});
            skLineSegment(sketch, "E23.8.4.3", {"start": v(-36.88, 31.39) * mm, "end": v(-34.53, 33.74) * mm});
            skLineSegment(sketch, "E23.8.5.0", {"start": v(-39.23, 24.74) * mm, "end": v(-36.88, 22.39) * mm});
            skLineSegment(sketch, "E23.8.5.1", {"start": v(-36.88, 27.1) * mm, "end": v(-39.23, 24.74) * mm});
            skLineSegment(sketch, "E23.8.5.2", {"start": v(-34.53, 24.74) * mm, "end": v(-36.88, 27.1) * mm});
            skLineSegment(sketch, "E23.8.5.3", {"start": v(-36.88, 22.39) * mm, "end": v(-34.53, 24.74) * mm});
            skLineSegment(sketch, "E23.8.6.0", {"start": v(-39.23, 15.74) * mm, "end": v(-36.88, 13.39) * mm});
            skLineSegment(sketch, "E23.8.6.1", {"start": v(-36.88, 18.1) * mm, "end": v(-39.23, 15.74) * mm});
            skLineSegment(sketch, "E23.8.6.2", {"start": v(-34.53, 15.74) * mm, "end": v(-36.88, 18.1) * mm});
            skLineSegment(sketch, "E23.8.6.3", {"start": v(-36.88, 13.39) * mm, "end": v(-34.53, 15.74) * mm});
            skLineSegment(sketch, "E23.8.7.0", {"start": v(-39.23, 6.74) * mm, "end": v(-36.88, 4.39) * mm});
            skLineSegment(sketch, "E23.8.7.1", {"start": v(-36.88, 9.1) * mm, "end": v(-39.23, 6.74) * mm});
            skLineSegment(sketch, "E23.8.7.2", {"start": v(-34.53, 6.74) * mm, "end": v(-36.88, 9.1) * mm});
            skLineSegment(sketch, "E23.8.7.3", {"start": v(-36.88, 4.39) * mm, "end": v(-34.53, 6.74) * mm});
            skLineSegment(sketch, "E23.9.0.0", {"start": v(-30.23, 69.74) * mm, "end": v(-27.88, 67.39) * mm});
            skLineSegment(sketch, "E23.9.0.1", {"start": v(-27.88, 72.1) * mm, "end": v(-30.23, 69.74) * mm});
            skLineSegment(sketch, "E23.9.0.2", {"start": v(-25.53, 69.74) * mm, "end": v(-27.88, 72.1) * mm});
            skLineSegment(sketch, "E23.9.0.3", {"start": v(-27.88, 67.39) * mm, "end": v(-25.53, 69.74) * mm});
            skLineSegment(sketch, "E23.9.1.0", {"start": v(-30.23, 60.74) * mm, "end": v(-27.88, 58.39) * mm});
            skLineSegment(sketch, "E23.9.1.1", {"start": v(-27.88, 63.1) * mm, "end": v(-30.23, 60.74) * mm});
            skLineSegment(sketch, "E23.9.1.2", {"start": v(-25.53, 60.74) * mm, "end": v(-27.88, 63.1) * mm});
            skLineSegment(sketch, "E23.9.1.3", {"start": v(-27.88, 58.39) * mm, "end": v(-25.53, 60.74) * mm});
            skLineSegment(sketch, "E23.9.2.0", {"start": v(-30.23, 51.74) * mm, "end": v(-27.88, 49.39) * mm});
            skLineSegment(sketch, "E23.9.2.1", {"start": v(-27.88, 54.1) * mm, "end": v(-30.23, 51.74) * mm});
            skLineSegment(sketch, "E23.9.2.2", {"start": v(-25.53, 51.74) * mm, "end": v(-27.88, 54.1) * mm});
            skLineSegment(sketch, "E23.9.2.3", {"start": v(-27.88, 49.39) * mm, "end": v(-25.53, 51.74) * mm});
            skLineSegment(sketch, "E23.9.3.0", {"start": v(-30.23, 42.74) * mm, "end": v(-27.88, 40.39) * mm});
            skLineSegment(sketch, "E23.9.3.1", {"start": v(-27.88, 45.1) * mm, "end": v(-30.23, 42.74) * mm});
            skLineSegment(sketch, "E23.9.3.2", {"start": v(-25.53, 42.74) * mm, "end": v(-27.88, 45.1) * mm});
            skLineSegment(sketch, "E23.9.3.3", {"start": v(-27.88, 40.39) * mm, "end": v(-25.53, 42.74) * mm});
            skLineSegment(sketch, "E23.9.4.0", {"start": v(-30.23, 33.74) * mm, "end": v(-27.88, 31.39) * mm});
            skLineSegment(sketch, "E23.9.4.1", {"start": v(-27.88, 36.1) * mm, "end": v(-30.23, 33.74) * mm});
            skLineSegment(sketch, "E23.9.4.2", {"start": v(-25.53, 33.74) * mm, "end": v(-27.88, 36.1) * mm});
            skLineSegment(sketch, "E23.9.4.3", {"start": v(-27.88, 31.39) * mm, "end": v(-25.53, 33.74) * mm});
            skLineSegment(sketch, "E23.9.5.0", {"start": v(-30.23, 24.74) * mm, "end": v(-27.88, 22.39) * mm});
            skLineSegment(sketch, "E23.9.5.1", {"start": v(-27.88, 27.1) * mm, "end": v(-30.23, 24.74) * mm});
            skLineSegment(sketch, "E23.9.5.2", {"start": v(-25.53, 24.74) * mm, "end": v(-27.88, 27.1) * mm});
            skLineSegment(sketch, "E23.9.5.3", {"start": v(-27.88, 22.39) * mm, "end": v(-25.53, 24.74) * mm});
            skLineSegment(sketch, "E23.9.6.0", {"start": v(-30.23, 15.74) * mm, "end": v(-27.88, 13.39) * mm});
            skLineSegment(sketch, "E23.9.6.1", {"start": v(-27.88, 18.1) * mm, "end": v(-30.23, 15.74) * mm});
            skLineSegment(sketch, "E23.9.6.2", {"start": v(-25.53, 15.74) * mm, "end": v(-27.88, 18.1) * mm});
            skLineSegment(sketch, "E23.9.6.3", {"start": v(-27.88, 13.39) * mm, "end": v(-25.53, 15.74) * mm});
            skLineSegment(sketch, "E23.9.7.0", {"start": v(-30.23, 6.74) * mm, "end": v(-27.88, 4.39) * mm});
            skLineSegment(sketch, "E23.9.7.1", {"start": v(-27.88, 9.1) * mm, "end": v(-30.23, 6.74) * mm});
            skLineSegment(sketch, "E23.9.7.2", {"start": v(-25.53, 6.74) * mm, "end": v(-27.88, 9.1) * mm});
            skLineSegment(sketch, "E23.9.7.3", {"start": v(-27.88, 4.39) * mm, "end": v(-25.53, 6.74) * mm});
            skLineSegment(sketch, "E23.10.0.0", {"start": v(-21.23, 69.74) * mm, "end": v(-18.88, 67.39) * mm});
            skLineSegment(sketch, "E23.10.0.1", {"start": v(-18.88, 72.1) * mm, "end": v(-21.23, 69.74) * mm});
            skLineSegment(sketch, "E23.10.0.2", {"start": v(-16.53, 69.74) * mm, "end": v(-18.88, 72.1) * mm});
            skLineSegment(sketch, "E23.10.0.3", {"start": v(-18.88, 67.39) * mm, "end": v(-16.53, 69.74) * mm});
            skLineSegment(sketch, "E23.10.1.0", {"start": v(-21.23, 60.74) * mm, "end": v(-18.88, 58.39) * mm});
            skLineSegment(sketch, "E23.10.1.1", {"start": v(-18.88, 63.1) * mm, "end": v(-21.23, 60.74) * mm});
            skLineSegment(sketch, "E23.10.1.2", {"start": v(-16.53, 60.74) * mm, "end": v(-18.88, 63.1) * mm});
            skLineSegment(sketch, "E23.10.1.3", {"start": v(-18.88, 58.39) * mm, "end": v(-16.53, 60.74) * mm});
            skLineSegment(sketch, "E23.10.2.0", {"start": v(-21.23, 51.74) * mm, "end": v(-18.88, 49.39) * mm});
            skLineSegment(sketch, "E23.10.2.1", {"start": v(-18.88, 54.1) * mm, "end": v(-21.23, 51.74) * mm});
            skLineSegment(sketch, "E23.10.2.2", {"start": v(-16.53, 51.74) * mm, "end": v(-18.88, 54.1) * mm});
            skLineSegment(sketch, "E23.10.2.3", {"start": v(-18.88, 49.39) * mm, "end": v(-16.53, 51.74) * mm});
            skLineSegment(sketch, "E23.10.3.0", {"start": v(-21.23, 42.74) * mm, "end": v(-18.88, 40.39) * mm});
            skLineSegment(sketch, "E23.10.3.1", {"start": v(-18.88, 45.1) * mm, "end": v(-21.23, 42.74) * mm});
            skLineSegment(sketch, "E23.10.3.2", {"start": v(-16.53, 42.74) * mm, "end": v(-18.88, 45.1) * mm});
            skLineSegment(sketch, "E23.10.3.3", {"start": v(-18.88, 40.39) * mm, "end": v(-16.53, 42.74) * mm});
            skLineSegment(sketch, "E23.10.4.0", {"start": v(-21.23, 33.74) * mm, "end": v(-18.88, 31.39) * mm});
            skLineSegment(sketch, "E23.10.4.1", {"start": v(-18.88, 36.1) * mm, "end": v(-21.23, 33.74) * mm});
            skLineSegment(sketch, "E23.10.4.2", {"start": v(-16.53, 33.74) * mm, "end": v(-18.88, 36.1) * mm});
            skLineSegment(sketch, "E23.10.4.3", {"start": v(-18.88, 31.39) * mm, "end": v(-16.53, 33.74) * mm});
            skLineSegment(sketch, "E23.10.5.0", {"start": v(-21.23, 24.74) * mm, "end": v(-18.88, 22.39) * mm});
            skLineSegment(sketch, "E23.10.5.1", {"start": v(-18.88, 27.1) * mm, "end": v(-21.23, 24.74) * mm});
            skLineSegment(sketch, "E23.10.5.2", {"start": v(-16.53, 24.74) * mm, "end": v(-18.88, 27.1) * mm});
            skLineSegment(sketch, "E23.10.5.3", {"start": v(-18.88, 22.39) * mm, "end": v(-16.53, 24.74) * mm});
            skLineSegment(sketch, "E23.10.6.0", {"start": v(-21.23, 15.74) * mm, "end": v(-18.88, 13.39) * mm});
            skLineSegment(sketch, "E23.10.6.1", {"start": v(-18.88, 18.1) * mm, "end": v(-21.23, 15.74) * mm});
            skLineSegment(sketch, "E23.10.6.2", {"start": v(-16.53, 15.74) * mm, "end": v(-18.88, 18.1) * mm});
            skLineSegment(sketch, "E23.10.6.3", {"start": v(-18.88, 13.39) * mm, "end": v(-16.53, 15.74) * mm});
            skLineSegment(sketch, "E23.10.7.0", {"start": v(-21.23, 6.74) * mm, "end": v(-18.88, 4.39) * mm});
            skLineSegment(sketch, "E23.10.7.1", {"start": v(-18.88, 9.1) * mm, "end": v(-21.23, 6.74) * mm});
            skLineSegment(sketch, "E23.10.7.2", {"start": v(-16.53, 6.74) * mm, "end": v(-18.88, 9.1) * mm});
            skLineSegment(sketch, "E23.10.7.3", {"start": v(-18.88, 4.39) * mm, "end": v(-16.53, 6.74) * mm});
            skLineSegment(sketch, "E23.11.0.0", {"start": v(-12.23, 69.74) * mm, "end": v(-9.88, 67.39) * mm});
            skLineSegment(sketch, "E23.11.0.1", {"start": v(-9.88, 72.1) * mm, "end": v(-12.23, 69.74) * mm});
            skLineSegment(sketch, "E23.11.0.2", {"start": v(-7.53, 69.74) * mm, "end": v(-9.88, 72.1) * mm});
            skLineSegment(sketch, "E23.11.0.3", {"start": v(-9.88, 67.39) * mm, "end": v(-7.53, 69.74) * mm});
            skLineSegment(sketch, "E23.11.1.0", {"start": v(-12.23, 60.74) * mm, "end": v(-9.88, 58.39) * mm});
            skLineSegment(sketch, "E23.11.1.1", {"start": v(-9.88, 63.1) * mm, "end": v(-12.23, 60.74) * mm});
            skLineSegment(sketch, "E23.11.1.2", {"start": v(-7.53, 60.74) * mm, "end": v(-9.88, 63.1) * mm});
            skLineSegment(sketch, "E23.11.1.3", {"start": v(-9.88, 58.39) * mm, "end": v(-7.53, 60.74) * mm});
            skLineSegment(sketch, "E23.11.2.0", {"start": v(-12.23, 51.74) * mm, "end": v(-9.88, 49.39) * mm});
            skLineSegment(sketch, "E23.11.2.1", {"start": v(-9.88, 54.1) * mm, "end": v(-12.23, 51.74) * mm});
            skLineSegment(sketch, "E23.11.2.2", {"start": v(-7.53, 51.74) * mm, "end": v(-9.88, 54.1) * mm});
            skLineSegment(sketch, "E23.11.2.3", {"start": v(-9.88, 49.39) * mm, "end": v(-7.53, 51.74) * mm});
            skLineSegment(sketch, "E23.11.3.0", {"start": v(-12.23, 42.74) * mm, "end": v(-9.88, 40.39) * mm});
            skLineSegment(sketch, "E23.11.3.1", {"start": v(-9.88, 45.1) * mm, "end": v(-12.23, 42.74) * mm});
            skLineSegment(sketch, "E23.11.3.2", {"start": v(-7.53, 42.74) * mm, "end": v(-9.88, 45.1) * mm});
            skLineSegment(sketch, "E23.11.3.3", {"start": v(-9.88, 40.39) * mm, "end": v(-7.53, 42.74) * mm});
            skLineSegment(sketch, "E23.11.4.0", {"start": v(-12.23, 33.74) * mm, "end": v(-9.88, 31.39) * mm});
            skLineSegment(sketch, "E23.11.4.1", {"start": v(-9.88, 36.1) * mm, "end": v(-12.23, 33.74) * mm});
            skLineSegment(sketch, "E23.11.4.2", {"start": v(-7.53, 33.74) * mm, "end": v(-9.88, 36.1) * mm});
            skLineSegment(sketch, "E23.11.4.3", {"start": v(-9.88, 31.39) * mm, "end": v(-7.53, 33.74) * mm});
            skLineSegment(sketch, "E23.11.5.0", {"start": v(-12.23, 24.74) * mm, "end": v(-9.88, 22.39) * mm});
            skLineSegment(sketch, "E23.11.5.1", {"start": v(-9.88, 27.1) * mm, "end": v(-12.23, 24.74) * mm});
            skLineSegment(sketch, "E23.11.5.2", {"start": v(-7.53, 24.74) * mm, "end": v(-9.88, 27.1) * mm});
            skLineSegment(sketch, "E23.11.5.3", {"start": v(-9.88, 22.39) * mm, "end": v(-7.53, 24.74) * mm});
            skLineSegment(sketch, "E23.11.6.0", {"start": v(-12.23, 15.74) * mm, "end": v(-9.88, 13.39) * mm});
            skLineSegment(sketch, "E23.11.6.1", {"start": v(-9.88, 18.1) * mm, "end": v(-12.23, 15.74) * mm});
            skLineSegment(sketch, "E23.11.6.2", {"start": v(-7.53, 15.74) * mm, "end": v(-9.88, 18.1) * mm});
            skLineSegment(sketch, "E23.11.6.3", {"start": v(-9.88, 13.39) * mm, "end": v(-7.53, 15.74) * mm});
            skLineSegment(sketch, "E23.11.7.0", {"start": v(-12.23, 6.74) * mm, "end": v(-9.88, 4.39) * mm});
            skLineSegment(sketch, "E23.11.7.1", {"start": v(-9.88, 9.1) * mm, "end": v(-12.23, 6.74) * mm});
            skLineSegment(sketch, "E23.11.7.2", {"start": v(-7.53, 6.74) * mm, "end": v(-9.88, 9.1) * mm});
            skLineSegment(sketch, "E23.11.7.3", {"start": v(-9.88, 4.39) * mm, "end": v(-7.53, 6.74) * mm});
            skLineSegment(sketch, "E23.direction1", {"start": v(-108.88, 67.39) * mm, "end": v(-99.88, 67.39) * mm, "construction": true});
            skLineSegment(sketch, "E23.direction2", {"start": v(-108.88, 67.39) * mm, "end": v(-108.88, 58.39) * mm, "construction": true});
            skSolve(sketch);
        }
        {
            var Q0;
            Q0 = qSketchRegion(id + "F2", true);
            extrude(context, id + "F3", {"entities" : qUnion([Q0]), "operationType" : NewBodyOperationType.ADD, "depth" : 5 * mm, "hasSecondDirection" : true, "secondDirectionOppositeDirection" : true, "secondDirectionDepth" : 5 * mm});
        }
    });
